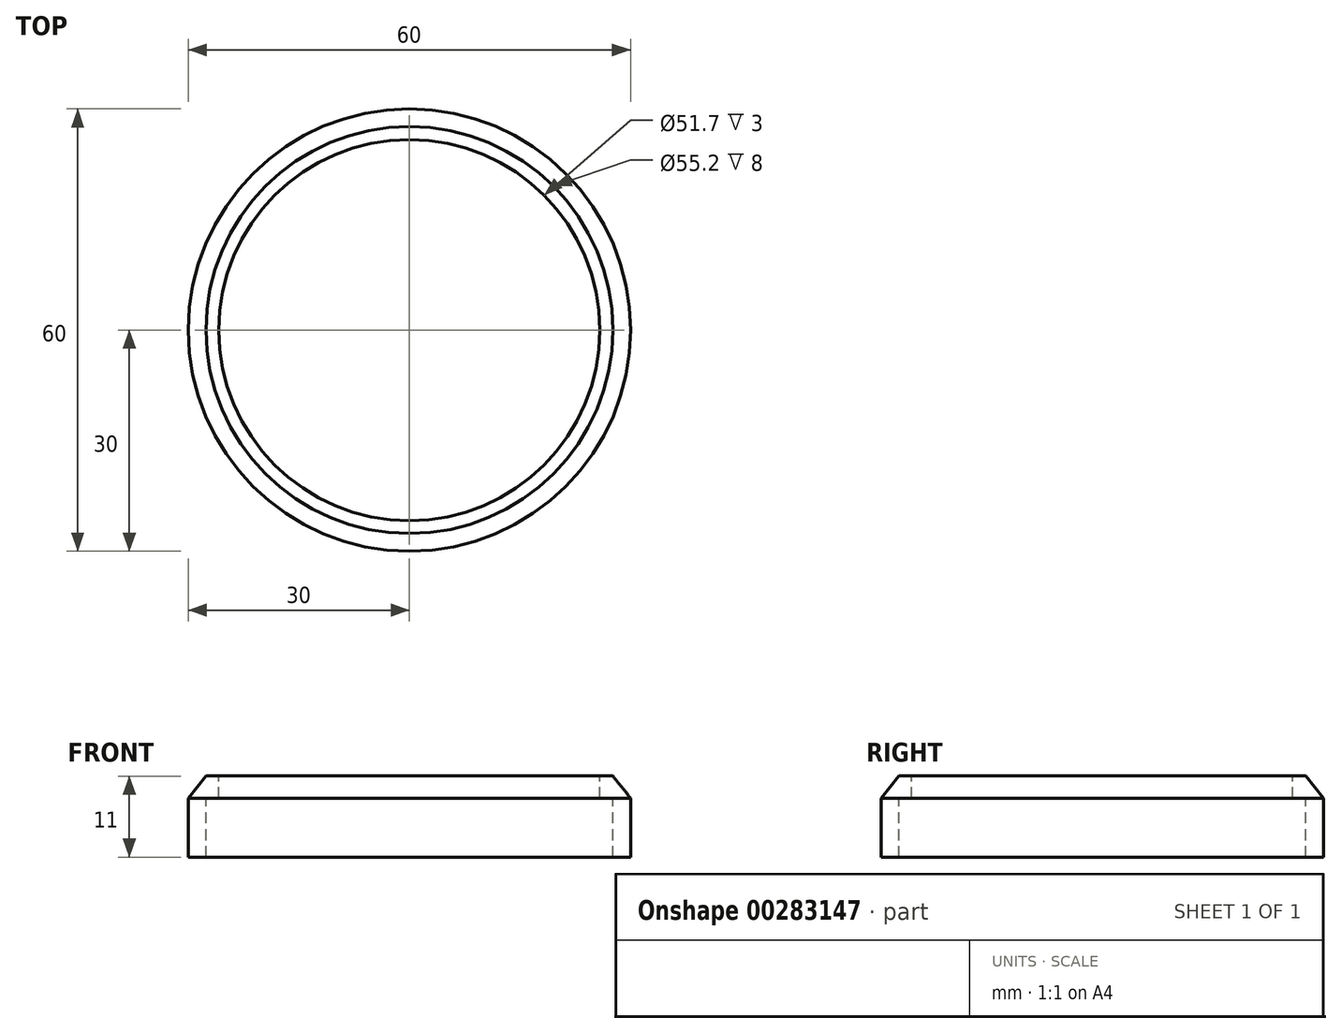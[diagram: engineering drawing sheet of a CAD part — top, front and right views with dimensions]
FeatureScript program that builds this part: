
annotation { "Feature Type Name" : "Feature", "Feature Type Description" : "" }
export const myFeature = defineFeature(function(context is Context, id is Id, definition is map)
    precondition{}
    {
        {
            var Q0;
            Q0=qCreatedBy(makeId("Front.planeOp"),FACE);
            var sketch = newSketch(context, id + "F0", { "sketchPlane" : qUnion([Q0])});
            skLineSegment(sketch, "E0", {"start": v(25.85, -24.37) * mm, "end": v(25.85, -27.37) * mm});
            skLineSegment(sketch, "E1", {"start": v(27.6, -27.37) * mm, "end": v(25.85, -27.37) * mm});
            skLineSegment(sketch, "E2", {"start": v(27.6, -27.37) * mm, "end": v(27.6, -35.37) * mm});
            skLineSegment(sketch, "E3", {"start": v(27.6, -35.37) * mm, "end": v(30, -35.37) * mm});
            skLineSegment(sketch, "E4", {"start": v(30, -35.37) * mm, "end": v(30, -27.37) * mm});
            skLineSegment(sketch, "E5", {"start": v(27.6, -24.37) * mm, "end": v(25.85, -24.37) * mm});
            skLineSegment(sketch, "E6", {"start": v(0, 24.42) * mm, "end": v(0, -13.18) * mm, "construction": true});
            skLineSegment(sketch, "E7", {"start": v(27.6, -24.37) * mm, "end": v(30, -27.37) * mm});
            skSolve(sketch);
        }
        {
            var Q0;
            Q0=makeQuery(id+"F0.imprint","IMPRINT",FACE,{"disambiguationData":[TD([[makeQuery(id+"F0.imprint","IMPRINT",EDGE,{"derivedFrom":sQuery(id+"F0.wireOp",EDGE,"E0")}),1.0]])]});
            var Q1;
            Q1=sQuery(id+"F0.wireOp",EDGE,"E6");
            revolve(context, id + "F1", {"entities" : qUnion([Q0]), "axis" : qUnion([Q1]), "revolveType" : RevolveType.FULL});
        }
    });
